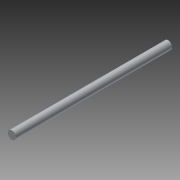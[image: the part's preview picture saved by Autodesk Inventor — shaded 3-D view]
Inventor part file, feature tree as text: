
AUTODESK INVENTOR PART (.ipt)
format: ipt  version: 2018 (Build 220112000, 112)  size: 99,840 bytes
history: native  units: in
note: dims shown in document units (in); Inventor stores cm internally (conversion verified against a paired STEP export)
features: extrude x1, sketch x1
ambient origin geometry x8: Origin, YZ Plane, XZ Plane, XY Plane, X Axis, Y Axis, Z Axis, Center Point
bodies: Solid1 (feature_tree)
feature tree (2):
  extrude  "Extrusion1"  Depth=12.0in TaperAngle=0.0deg
  sketch  "Sketch1"  dims[d0=0.625in d1=12.0in d2=0.0in]
